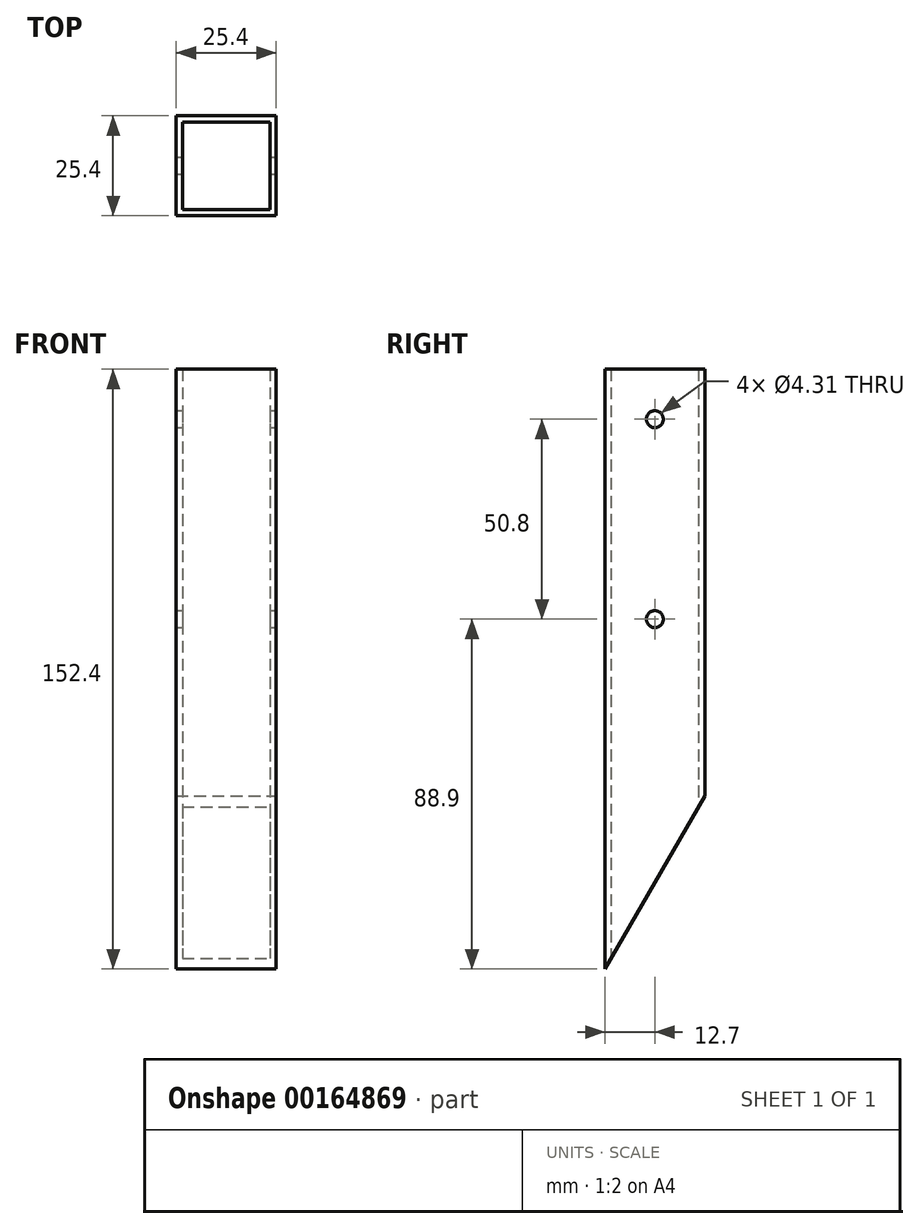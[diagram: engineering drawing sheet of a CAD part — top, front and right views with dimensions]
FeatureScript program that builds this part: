
annotation { "Feature Type Name" : "Feature", "Feature Type Description" : "" }
export const myFeature = defineFeature(function(context is Context, id is Id, definition is map)
    precondition{}
    {
        {
            var Q0;
            Q0=qCreatedBy(makeId("Top.planeOp"),FACE);
            var sketch = newSketch(context, id + "F0", { "sketchPlane" : qUnion([Q0])});
            skLineSegment(sketch, "E0.bottom", {"start": v(11.11, -11.11) * mm, "end": v(-11.11, -11.11) * mm});
            skLineSegment(sketch, "E0.top", {"start": v(11.11, 11.11) * mm, "end": v(-11.11, 11.11) * mm});
            skLineSegment(sketch, "E0.left", {"start": v(11.11, -11.11) * mm, "end": v(11.11, 11.11) * mm});
            skLineSegment(sketch, "E0.right", {"start": v(-11.11, -11.11) * mm, "end": v(-11.11, 11.11) * mm});
            skPoint(sketch, "E0.middle", {"position": v(0, 0) * mm});
            skLineSegment(sketch, "E1.bottom", {"start": v(12.7, -12.7) * mm, "end": v(-12.7, -12.7) * mm});
            skLineSegment(sketch, "E1.top", {"start": v(12.7, 12.7) * mm, "end": v(-12.7, 12.7) * mm});
            skLineSegment(sketch, "E1.left", {"start": v(12.7, -12.7) * mm, "end": v(12.7, 12.7) * mm});
            skLineSegment(sketch, "E1.right", {"start": v(-12.7, -12.7) * mm, "end": v(-12.7, 12.7) * mm});
            skSolve(sketch);
        }
        {
            var Q0;
            Q0=qSketchRegion(id+"F0",true);
            extrude(context, id + "F1", {"entities" : qUnion([Q0]), "depth" : 152.4 * mm});
        }
        {
            var Q0;
            Q0=makeQuery(id+"F1.opExtrude","SWEPT_FACE",FACE,{"disambiguationData":[OSD([sQuery(id+"F0.wireOp",EDGE,"E1.left")])]});
            var sketch = newSketch(context, id + "F2", { "sketchPlane" : qUnion([Q0])});
            skLineSegment(sketch, "E2.bottom", {"start": v(-12.7, 0) * mm, "end": v(12.7, 0) * mm});
            skLineSegment(sketch, "E2.top", {"start": v(-12.7, 44) * mm, "end": v(12.7, 44) * mm, "construction": true});
            skLineSegment(sketch, "E2.left", {"start": v(-12.7, 0) * mm, "end": v(-12.7, 44) * mm, "construction": true});
            skLineSegment(sketch, "E2.right", {"start": v(12.7, 0) * mm, "end": v(12.7, 44) * mm});
            skLineSegment(sketch, "E3", {"start": v(-12.7, 0) * mm, "end": v(12.7, 44) * mm});
            skSolve(sketch);
        }
        {
            var Q0;
            Q0=qSketchRegion(id+"F2",true);
            var Q1;
            Q1=makeQuery(id+"F1.opExtrude","SWEPT_FACE",FACE,{"disambiguationData":[OSD([sQuery(id+"F0.wireOp",EDGE,"E1.right")])]});
            extrude(context, id + "F3", {"entities" : qUnion([Q0]), "operationType" : NewBodyOperationType.REMOVE, "endBound" : BoundingType.UP_TO_SURFACE, "oppositeDirection" : true, "endBoundEntityFace" : qUnion([Q1]), "depth" : 25.4 * mm});
        }
        {
            var Q0;
            Q0=makeQuery(id+"F1.opExtrude","SWEPT_FACE",FACE,{"disambiguationData":[OSD([sQuery(id+"F0.wireOp",EDGE,"E1.left")])]});
            var sketch = newSketch(context, id + "F4", { "sketchPlane" : qUnion([Q0])});
            skLineSegment(sketch, "E4.bottom", {"start": v(0, 152.4) * mm, "end": v(-12.7, 152.4) * mm, "construction": true});
            skLineSegment(sketch, "E4.top", {"start": v(0, 139.7) * mm, "end": v(-12.7, 139.7) * mm, "construction": true});
            skLineSegment(sketch, "E4.left", {"start": v(0, 152.4) * mm, "end": v(0, 139.7) * mm, "construction": true});
            skLineSegment(sketch, "E4.right", {"start": v(-12.7, 152.4) * mm, "end": v(-12.7, 139.7) * mm, "construction": true});
            skLineSegment(sketch, "E5", {"start": v(0, 139.7) * mm, "end": v(0, 88.9) * mm, "construction": true});
            skCircle(sketch, "E6", {"center": v(0, 139.7) * mm, "radius": 2.15 * mm});
            skCircle(sketch, "E7", {"center": v(0, 88.9) * mm, "radius": 2.15 * mm});
            skSolve(sketch);
        }
        {
            var Q0;
            Q0 = qSketchRegion(id + "F4", true);
            var Q1;
            Q1=makeQuery(id+"F1.opExtrude","SWEPT_FACE",FACE,{"disambiguationData":[OSD([sQuery(id+"F0.wireOp",EDGE,"E1.right")])]});
            extrude(context, id + "F5", {"entities" : qUnion([Q0]), "operationType" : NewBodyOperationType.REMOVE, "endBound" : BoundingType.UP_TO_SURFACE, "oppositeDirection" : true, "endBoundEntityFace" : qUnion([Q1]), "depth" : 25.4 * mm});
        }
    });
